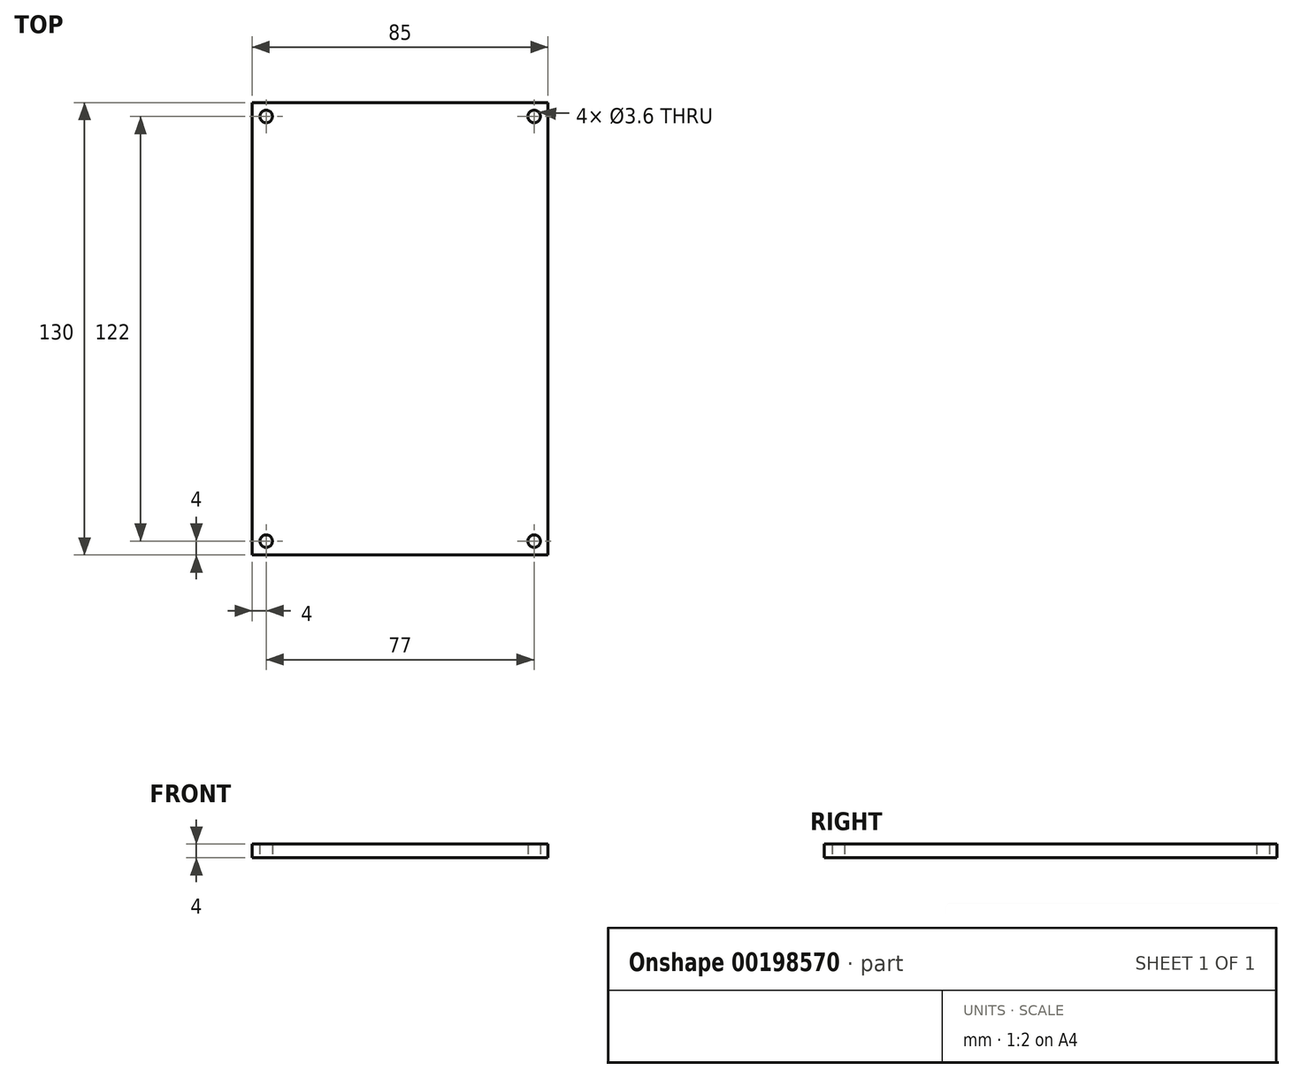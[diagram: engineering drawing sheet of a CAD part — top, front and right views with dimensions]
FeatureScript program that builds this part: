
annotation { "Feature Type Name" : "Feature", "Feature Type Description" : "" }
export const myFeature = defineFeature(function(context is Context, id is Id, definition is map)
    precondition{}
    {
        {
            assignVariable(context, id + "F0", {"name" : "HoleDiameter", "anyValue" : 3.6});
        }
        {
            assignVariable(context, id + "F1", {"name" : "PCB_Thickness", "anyValue" : 4});
        }
        {
            var Q0;
            Q0=qCreatedBy(makeId("Top.planeOp"),FACE);
            var sketch = newSketch(context, id + "F2", { "sketchPlane" : qUnion([Q0])});
            skLineSegment(sketch, "E0.bottom", {"start": v(42.5, 65) * mm, "end": v(-42.5, 65) * mm});
            skLineSegment(sketch, "E0.top", {"start": v(42.5, -65) * mm, "end": v(-42.5, -65) * mm});
            skLineSegment(sketch, "E0.left", {"start": v(42.5, 65) * mm, "end": v(42.5, -65) * mm});
            skLineSegment(sketch, "E0.right", {"start": v(-42.5, 65) * mm, "end": v(-42.5, -65) * mm});
            skPoint(sketch, "E0.middle", {"position": v(0, 0) * mm});
            skLineSegment(sketch, "E1", {"start": v(0, -65) * mm, "end": v(0, 65) * mm, "construction": true});
            skLineSegment(sketch, "E2", {"start": v(-42.5, 0) * mm, "end": v(42.5, 0) * mm, "construction": true});
            skPoint(sketch, "E3", {"position": v(-38.5, 61) * mm});
            skPoint(sketch, "E4", {"position": v(38.5, 61) * mm});
            skPoint(sketch, "E5", {"position": v(-38.5, -61) * mm});
            skPoint(sketch, "E6", {"position": v(38.5, -61) * mm});
            skSolve(sketch);
        }
        {
            var Q0;
            Q0 = qSketchRegion(id + "F2", true);
            extrude(context, id + "F3", {"entities" : qUnion([Q0]), "depth" : (getVariable(context, 'PCB_Thickness')) * mm});
        }
        {
            var Q0;
            Q0=sQuery(id+"F2.wireOp",VERTEX,"E4");
            var Q1;
            Q1=sQuery(id+"F2.wireOp",VERTEX,"E6");
            var Q2;
            Q2=sQuery(id+"F2.wireOp",VERTEX,"E5");
            var Q3;
            Q3=sQuery(id+"F2.wireOp",VERTEX,"E3");
            var Q4;
            Q4=makeQuery(id+"F3.opExtrude","SWEPT_BODY",BODY,{"disambiguationData":[OSD([sQuery(id+"F2.wireOp",EDGE,"E0.bottom"),sQuery(id+"F2.wireOp",EDGE,"E0.top"),sQuery(id+"F2.wireOp",EDGE,"E0.left"),sQuery(id+"F2.wireOp",EDGE,"E0.right")])]});
            hole(context, id + "F4", {"style" : HoleStyle.SIMPLE, "endStyle" : HoleEndStyle.BLIND, "oppositeDirection" : true, "holeDiameter" : (getVariable(context, 'HoleDiameter')) * mm, "holeDepth" : (getVariable(context, 'PCB_Thickness')) * mm, "startFromSketch" : true, "locations" : qUnion([Q0, Q1, Q2, Q3]), "scope" : qUnion([Q4])});
        }
        {
            assignVariable(context, id + "F5", {"name" : "Case_Spacers", "anyValue" : 5});
        }
        {
            var Q0;
            Q0=qCreatedBy(makeId("Top.planeOp"),FACE);
            cPlane(context, id + "F6", {"entities" : qUnion([Q0]), "cplaneType" : CPlaneType.OFFSET, "offset" : (getVariable(context, 'Case_Spacers')) * mm, "oppositeDirection" : true, "width" : 150 * mm, "height" : 150 * mm});
        }
    });
